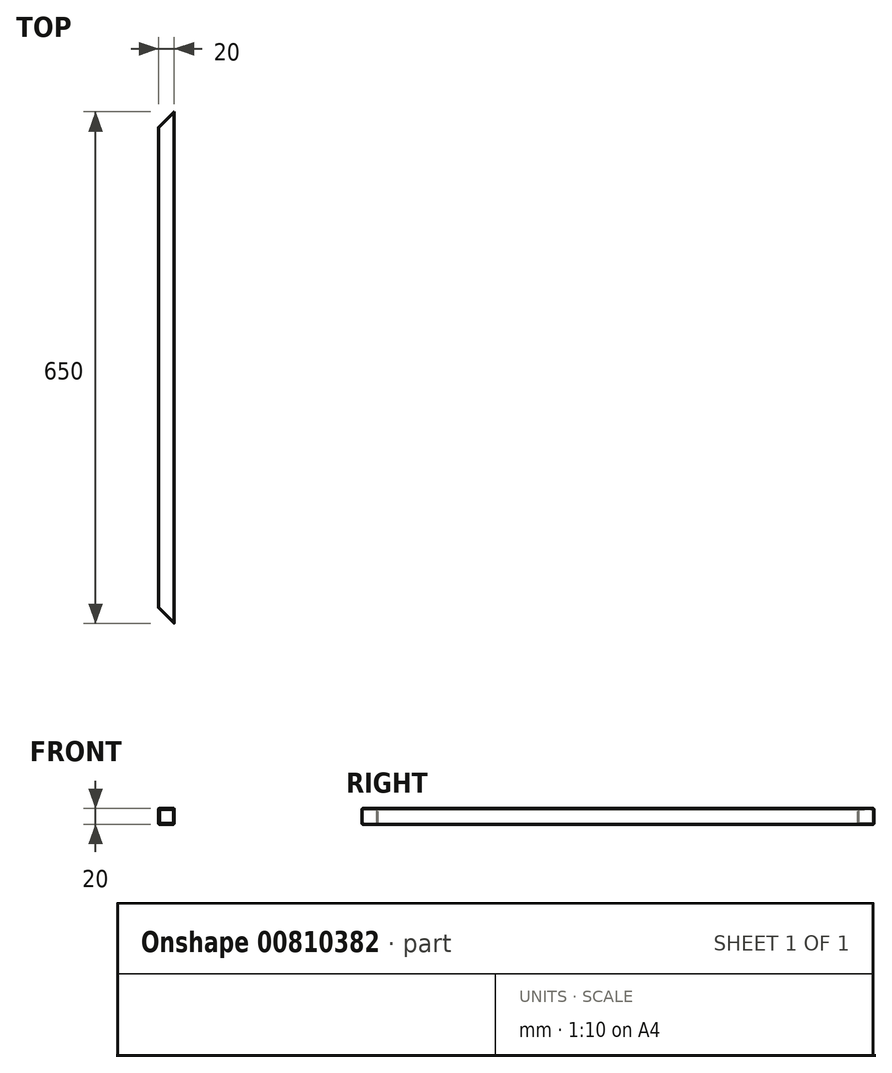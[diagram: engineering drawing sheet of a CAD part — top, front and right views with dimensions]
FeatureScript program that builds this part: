
annotation { "Feature Type Name" : "Feature", "Feature Type Description" : "" }
export const myFeature = defineFeature(function(context is Context, id is Id, definition is map)
    precondition{}
    {
        {
            var Q0;
            Q0=qCreatedBy(makeId("Front.planeOp"),FACE);
            var sketch = newSketch(context, id + "F0", { "sketchPlane" : qUnion([Q0])});
            skLineSegment(sketch, "E0.bottom", {"start": v(-9, 10) * mm, "end": v(9, 10) * mm});
            skLineSegment(sketch, "E0.top", {"start": v(-9, -10) * mm, "end": v(9, -10) * mm});
            skLineSegment(sketch, "E0.left", {"start": v(-10, 9) * mm, "end": v(-10, -9) * mm});
            skLineSegment(sketch, "E0.right", {"start": v(10, 9) * mm, "end": v(10, -9) * mm});
            skPoint(sketch, "E0.middle", {"position": v(0, 0) * mm});
            skLineSegment(sketch, "E1.bottom", {"start": v(-7.75, 8.75) * mm, "end": v(7.75, 8.75) * mm});
            skLineSegment(sketch, "E1.top", {"start": v(-7.75, -8.75) * mm, "end": v(7.75, -8.75) * mm});
            skLineSegment(sketch, "E1.left", {"start": v(-8.75, 7.75) * mm, "end": v(-8.75, -7.75) * mm});
            skLineSegment(sketch, "E1.right", {"start": v(8.75, 7.75) * mm, "end": v(8.75, -7.75) * mm});
            skPoint(sketch, "E2.visualSharp", {"position": v(-10, 10) * mm});
            skArc(sketch, "E2.filletArc", {"start": v(-9, 10) * mm, "mid": v(-9.7, 9.7) * mm, "end": v(-10, 9) * mm});
            skPoint(sketch, "E3.visualSharp", {"position": v(-10, -10) * mm});
            skArc(sketch, "E3.filletArc", {"start": v(-10, -9) * mm, "mid": v(-9.7, -9.7) * mm, "end": v(-9, -10) * mm});
            skPoint(sketch, "E4.visualSharp", {"position": v(-8.75, -8.75) * mm});
            skArc(sketch, "E4.filletArc", {"start": v(-8.75, -7.75) * mm, "mid": v(-8.46, -8.46) * mm, "end": v(-7.75, -8.75) * mm});
            skPoint(sketch, "E5.visualSharp", {"position": v(-8.75, 8.75) * mm});
            skArc(sketch, "E5.filletArc", {"start": v(-7.75, 8.75) * mm, "mid": v(-8.46, 8.46) * mm, "end": v(-8.75, 7.75) * mm});
            skPoint(sketch, "E6.visualSharp", {"position": v(8.75, 8.75) * mm});
            skArc(sketch, "E6.filletArc", {"start": v(8.75, 7.75) * mm, "mid": v(8.46, 8.46) * mm, "end": v(7.75, 8.75) * mm});
            skPoint(sketch, "E7.visualSharp", {"position": v(8.75, -8.75) * mm});
            skArc(sketch, "E7.filletArc", {"start": v(7.75, -8.75) * mm, "mid": v(8.46, -8.46) * mm, "end": v(8.75, -7.75) * mm});
            skPoint(sketch, "E8.visualSharp", {"position": v(10, -10) * mm});
            skArc(sketch, "E8.filletArc", {"start": v(9, -10) * mm, "mid": v(9.7, -9.7) * mm, "end": v(10, -9) * mm});
            skPoint(sketch, "E9.visualSharp", {"position": v(10, 10) * mm});
            skArc(sketch, "E9.filletArc", {"start": v(10, 9) * mm, "mid": v(9.7, 9.7) * mm, "end": v(9, 10) * mm});
            skSolve(sketch);
        }
        {
            var Q0;
            Q0=makeQuery(id+"F0.imprint","IMPRINT",FACE,{"disambiguationData":[TD([[makeQuery(id+"F0.imprint","IMPRINT",EDGE,{"derivedFrom":sQuery(id+"F0.wireOp",EDGE,"E0.bottom")}),-1.0]])]});
            extrude(context, id + "F1", {"entities" : qUnion([Q0]), "depth" : 650 * mm, "offsetDistance" : 25 * mm});
        }
        {
            var Q0;
            Q0=makeQuery(id+"F1.opExtrude","SWEPT_FACE",FACE,{"disambiguationData":[OSD([sQuery(id+"F0.wireOp",EDGE,"E0.bottom")])]});
            var sketch = newSketch(context, id + "F2", { "sketchPlane" : qUnion([Q0])});
            skLineSegment(sketch, "E10", {"start": v(9, -650) * mm, "end": v(10, -650) * mm});
            skLineSegment(sketch, "E11", {"start": v(10, -650) * mm, "end": v(-10, -630) * mm});
            skLineSegment(sketch, "E12", {"start": v(-10, -630) * mm, "end": v(-10, -650) * mm});
            skLineSegment(sketch, "E13", {"start": v(-10, -650) * mm, "end": v(-9, -650) * mm});
            skLineSegment(sketch, "E14", {"start": v(-9, -650) * mm, "end": v(9, -650) * mm});
            skLineSegment(sketch, "E15", {"start": v(-9, -325) * mm, "end": v(9, -325) * mm, "construction": true});
            skLineSegment(sketch, "E16.MirrorCS", {"start": v(9, 0) * mm, "end": v(10, 0) * mm});
            skLineSegment(sketch, "E17.MirrorCS", {"start": v(-10, 0) * mm, "end": v(-9, 0) * mm});
            skLineSegment(sketch, "E18.MirrorCS", {"start": v(-10, -20) * mm, "end": v(-10, 0) * mm});
            skLineSegment(sketch, "E19.MirrorCS", {"start": v(10, 0) * mm, "end": v(-10, -20) * mm});
            skLineSegment(sketch, "E20.MirrorCS", {"start": v(-9, 0) * mm, "end": v(9, 0) * mm});
            skSolve(sketch);
        }
        {
            var Q0;
            {var subQ6=sQuery(id+"F2.wireOp",EDGE,"E14");Q0=makeQuery(id+"F2.imprint","IMPRINT",FACE,{"disambiguationData":[TD([[makeQuery(id+"F2.imprint","IMPRINT",EDGE,{"derivedFrom":subQ6}),1.0]])]});}
            var Q1;
            {var subQ0=sQuery(id+"F2.wireOp",EDGE,"E12");Q1=makeQuery(id+"F2.imprint","IMPRINT",FACE,{"disambiguationData":[TD([[makeQuery(id+"F2.imprint","IMPRINT",EDGE,{"derivedFrom":subQ0}),1.0]])]});}
            var Q2;
            {var subQ0=sQuery(id+"F2.wireOp",EDGE,"E10");Q2=makeQuery(id+"F2.imprint","IMPRINT",FACE,{"disambiguationData":[TD([[makeQuery(id+"F2.imprint","IMPRINT",EDGE,{"derivedFrom":subQ0}),1.0]])]});}
            var Q3;
            {var subQ0=sQuery(id+"F2.wireOp",EDGE,"E16.MirrorCS");Q3=makeQuery(id+"F2.imprint","IMPRINT",FACE,{"disambiguationData":[TD([[makeQuery(id+"F2.imprint","IMPRINT",EDGE,{"derivedFrom":subQ0}),-1.0]])]});}
            var Q4;
            {var subQ6=sQuery(id+"F2.wireOp",EDGE,"E20.MirrorCS");Q4=makeQuery(id+"F2.imprint","IMPRINT",FACE,{"disambiguationData":[TD([[makeQuery(id+"F2.imprint","IMPRINT",EDGE,{"derivedFrom":subQ6}),-1.0]])]});}
            var Q5;
            {var subQ0=sQuery(id+"F2.wireOp",EDGE,"E17.MirrorCS");Q5=makeQuery(id+"F2.imprint","IMPRINT",FACE,{"disambiguationData":[TD([[makeQuery(id+"F2.imprint","IMPRINT",EDGE,{"derivedFrom":subQ0}),-1.0]])]});}
            extrude(context, id + "F3", {"entities" : qUnion([Q0, Q1, Q2, Q3, Q4, Q5]), "operationType" : NewBodyOperationType.REMOVE, "oppositeDirection" : true, "depth" : 20 * mm, "offsetDistance" : 25 * mm});
        }
    });
